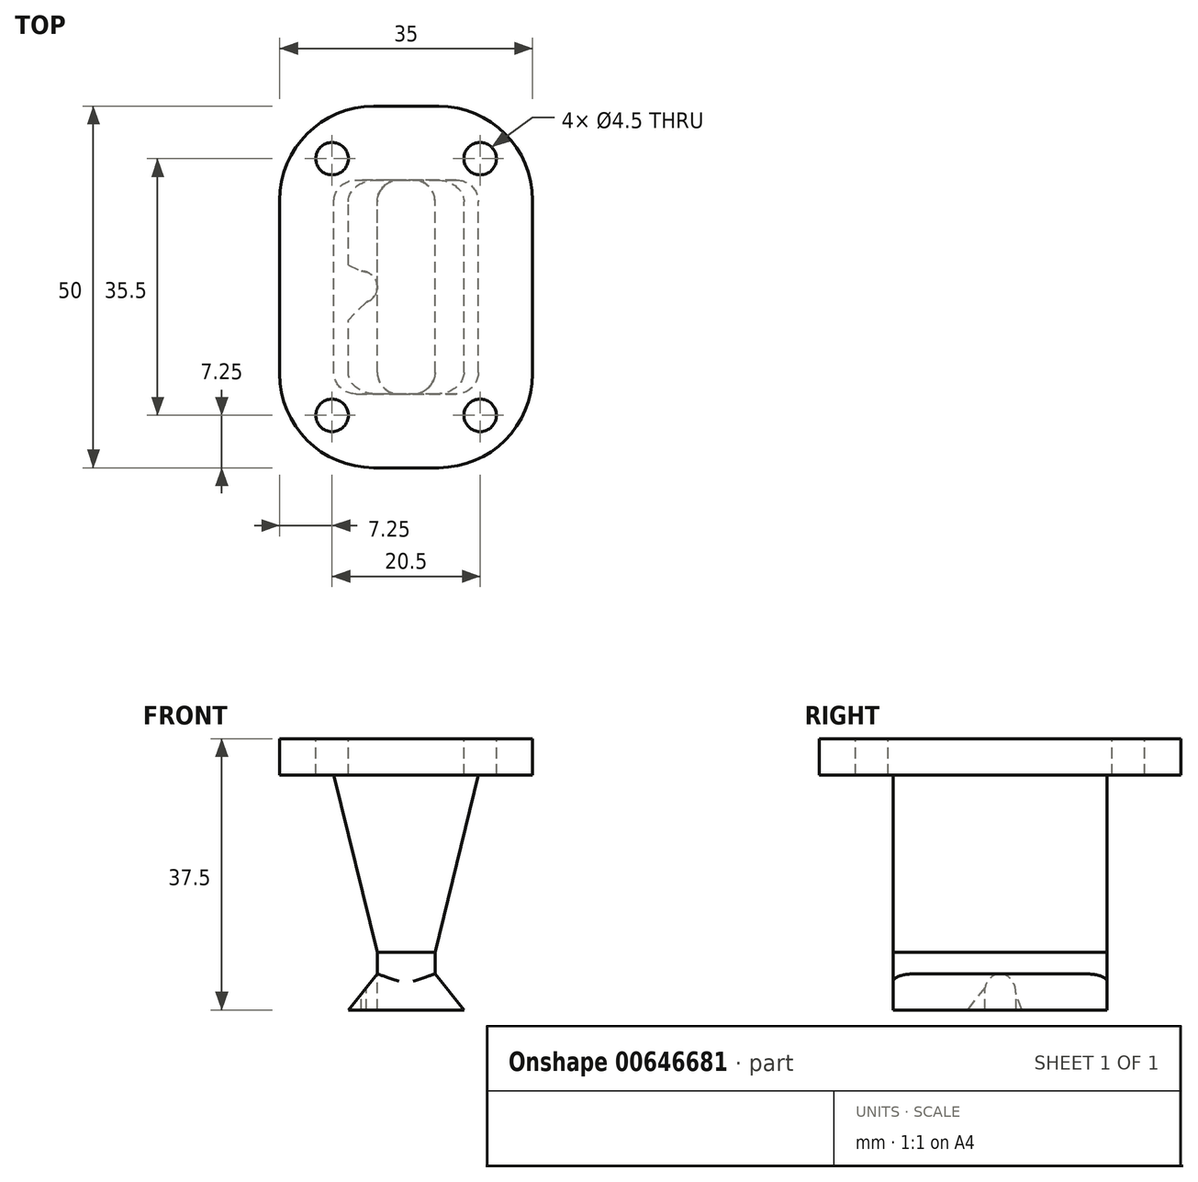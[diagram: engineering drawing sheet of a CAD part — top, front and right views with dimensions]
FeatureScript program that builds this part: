
annotation { "Feature Type Name" : "Feature", "Feature Type Description" : "" }
export const myFeature = defineFeature(function(context is Context, id is Id, definition is map)
    precondition{}
    {
        {
            var Q0;
            Q0=qCreatedBy(makeId("Front.planeOp"),FACE);
            var sketch = newSketch(context, id + "F0", { "sketchPlane" : qUnion([Q0])});
            skLineSegment(sketch, "E0", {"start": v(0, 0) * mm, "end": v(4, 0) * mm});
            skLineSegment(sketch, "E1", {"start": v(0, 0) * mm, "end": v(-4, 0) * mm});
            skLineSegment(sketch, "E2", {"start": v(0, 0) * mm, "end": v(0, -7.5) * mm, "construction": true});
            skLineSegment(sketch, "E3", {"start": v(0, -7.5) * mm, "end": v(8, -7.5) * mm});
            skLineSegment(sketch, "E4", {"start": v(4, 0) * mm, "end": v(4, -2.5) * mm});
            skLineSegment(sketch, "E5", {"start": v(4, -2.5) * mm, "end": v(8, -7.5) * mm});
            skLineSegment(sketch, "E6.MirrorCS", {"start": v(-4, 0) * mm, "end": v(-4, -2.5) * mm});
            skLineSegment(sketch, "E7.MirrorCS", {"start": v(-4, -2.5) * mm, "end": v(-8, -7.5) * mm});
            skLineSegment(sketch, "E8.MirrorCS", {"start": v(0, -7.5) * mm, "end": v(-8, -7.5) * mm});
            skSolve(sketch);
        }
        {
            var Q0;
            Q0=makeQuery(id+"F0.imprint","IMPRINT",FACE,{"disambiguationData":[TD([[makeQuery(id+"F0.imprint","IMPRINT",EDGE,{"derivedFrom":sQuery(id+"F0.wireOp",EDGE,"E0")}),-1.0]])]});
            extrude(context, id + "F1", {"entities" : qUnion([Q0]), "depth" : 29.6 * mm, "offsetDistance" : 25 * mm});
        }
        {
            var Q0;
            Q0=makeQuery(id+"F1.opExtrude","SWEPT_FACE",FACE,{"disambiguationData":[OSD([sQuery(id+"F0.wireOp",EDGE,"E0"),sQuery(id+"F0.wireOp",EDGE,"E1")])]});
            var sketch = newSketch(context, id + "F2", { "sketchPlane" : qUnion([Q0])});
            skLineSegment(sketch, "E9", {"start": v(-4, -14.8) * mm, "end": v(4, -14.8) * mm, "construction": true});
            skLineSegment(sketch, "E10.0", {"start": v(-8, -29.6) * mm, "end": v(-8, 0) * mm, "construction": true});
            skLineSegment(sketch, "E11", {"start": v(-6.2, -14.8) * mm, "end": v(-8, -14.8) * mm, "construction": true});
            skLineSegment(sketch, "E12", {"start": v(-8, -14.8) * mm, "end": v(-8, -18.8) * mm});
            skLineSegment(sketch, "E13", {"start": v(-8, -18.8) * mm, "end": v(-4, -14.8) * mm, "construction": true});
            skLineSegment(sketch, "E14.0", {"start": v(-3.03, -14.4) * mm, "end": v(-4.04, -14.4) * mm, "construction": true});
            skLineSegment(sketch, "E14.1", {"start": v(-8.17, -19.53) * mm, "end": v(-5.53, -16.9) * mm});
            skLineSegment(sketch, "E15", {"start": v(-8, -19.37) * mm, "end": v(-8.17, -19.53) * mm});
            skLineSegment(sketch, "E16", {"start": v(-8, -19.37) * mm, "end": v(-8, -14.4) * mm});
            skLineSegment(sketch, "E17", {"start": v(-4, -14.4) * mm, "end": v(-4, -15.37) * mm});
            skLineSegment(sketch, "E18", {"start": v(-4, -14.8) * mm, "end": v(-6.2, -14.8) * mm});
            skArc(sketch, "E19", {"start": v(-6.2, -17) * mm, "mid": v(-4, -14.8) * mm, "end": v(-6.2, -12.6) * mm});
            skLineSegment(sketch, "E20.trimOffspring", {"start": v(-4.1, -15.47) * mm, "end": v(-3.03, -14.4) * mm, "construction": true});
            skLineSegment(sketch, "E21", {"start": v(-6.2, -14.8) * mm, "end": v(-6.2, -12.6) * mm, "construction": true});
            skLineSegment(sketch, "E22", {"start": v(-9.1, -11.27) * mm, "end": v(-9.1, -19.39) * mm});
            skLineSegment(sketch, "E23", {"start": v(-9.1, -19.39) * mm, "end": v(-8, -19.37) * mm});
            skLineSegment(sketch, "E24", {"start": v(-6.2, -12.6) * mm, "end": v(-9.1, -11.27) * mm});
            skSolve(sketch);
        }
        {
            var Q0;
            {var subQ3=sQuery(id+"F2.wireOp",EDGE,"E14.1");Q0=makeQuery(id+"F2.imprint","IMPRINT",FACE,{"disambiguationData":[TD([[makeQuery(id+"F2.imprint","IMPRINT",EDGE,{"derivedFrom":subQ3}),1.0]])]});}
            extrude(context, id + "F3", {"entities" : qUnion([Q0]), "operationType" : NewBodyOperationType.REMOVE, "oppositeDirection" : true, "depth" : 25 * mm, "offsetDistance" : 25 * mm});
        }
        {
            var Q0;
            {var subQ0=sQuery(id+"F0.wireOp",EDGE,"E0");Q0=makeQuery(id+"F2.imprint","IMPRINT",FACE,{"disambiguationData":[TD([[makeQuery(id+"F2.imprint","IMPRINT",EDGE,{"derivedFrom":makeQuery(id+"F1.opExtrude","SWEPT_EDGE",EDGE,{"disambiguationData":[OSD([subQ0,sQuery(id+"F0.wireOp",EDGE,"E4")])]})}),1.0]])]});}
            cPlane(context, id + "F4", {"entities" : qUnion([Q0]), "cplaneType" : CPlaneType.OFFSET, "offset" : 30 * mm, "width" : 150 * mm, "height" : 150 * mm});
        }
        {
            var Q0;
            Q0=qCreatedBy(id+"F4.planeOp",FACE);
            var sketch = newSketch(context, id + "F5", { "sketchPlane" : qUnion([Q0])});
            skPoint(sketch, "E25.0", {"position": v(0, -14.8) * mm});
            skLineSegment(sketch, "E26.0.1", {"start": v(-4, -15.37) * mm, "end": v(-4, -29.6) * mm, "construction": true});
            skLineSegment(sketch, "E26.0.2", {"start": v(-4, -29.6) * mm, "end": v(4, -29.6) * mm, "construction": true});
            skLineSegment(sketch, "E26.0.3", {"start": v(4, -29.6) * mm, "end": v(4, 0) * mm, "construction": true});
            skLineSegment(sketch, "E26.0.4", {"start": v(4, 0) * mm, "end": v(-4, 0) * mm, "construction": true});
            skLineSegment(sketch, "E26.0.5", {"start": v(-4, 0) * mm, "end": v(-4, -14.4) * mm, "construction": true});
            skLineSegment(sketch, "E27", {"start": v(-4, -14.4) * mm, "end": v(-4, -15.37) * mm, "construction": true});
            skLineSegment(sketch, "E28.bottom", {"start": v(17.5, -39.8) * mm, "end": v(-17.5, -39.8) * mm});
            skLineSegment(sketch, "E28.top", {"start": v(17.5, 10.2) * mm, "end": v(-17.5, 10.2) * mm});
            skLineSegment(sketch, "E28.left", {"start": v(17.5, -39.8) * mm, "end": v(17.5, 10.2) * mm});
            skLineSegment(sketch, "E28.right", {"start": v(-17.5, -39.8) * mm, "end": v(-17.5, 10.2) * mm});
            skLineSegment(sketch, "E29.bottom", {"start": v(8, -30.3) * mm, "end": v(-8, -30.3) * mm, "construction": true});
            skLineSegment(sketch, "E29.top", {"start": v(8, 0.7) * mm, "end": v(-8, 0.7) * mm, "construction": true});
            skLineSegment(sketch, "E29.left", {"start": v(8, -30.3) * mm, "end": v(8, 0.7) * mm, "construction": true});
            skLineSegment(sketch, "E29.right", {"start": v(-8, -30.3) * mm, "end": v(-8, 0.7) * mm, "construction": true});
            skLineSegment(sketch, "E30", {"start": v(8, 0.7) * mm, "end": v(8, 5.2) * mm, "construction": true});
            skLineSegment(sketch, "E31", {"start": v(8, 5.2) * mm, "end": v(12.5, 5.2) * mm, "construction": true});
            skLineSegment(sketch, "E32", {"start": v(12.5, 5.2) * mm, "end": v(12.5, 0.7) * mm, "construction": true});
            skLineSegment(sketch, "E33", {"start": v(12.5, 0.7) * mm, "end": v(8, 0.7) * mm, "construction": true});
            skLineSegment(sketch, "E34", {"start": v(10.25, 5.2) * mm, "end": v(10.25, 0.7) * mm, "construction": true});
            skCircle(sketch, "E35", {"center": v(10.25, 2.95) * mm, "radius": 2.25 * mm});
            skLineSegment(sketch, "E36", {"start": v(0, -14.8) * mm, "end": v(0, -12.15) * mm, "construction": true});
            skLineSegment(sketch, "E37", {"start": v(0, -14.8) * mm, "end": v(2.16, -14.8) * mm, "construction": true});
            skCircle(sketch, "E38.MirrorC", {"center": v(10.25, -32.55) * mm, "radius": 2.25 * mm});
            skCircle(sketch, "E39.MirrorC", {"center": v(-10.25, 2.95) * mm, "radius": 2.25 * mm});
            skCircle(sketch, "E40.MirrorC", {"center": v(-10.25, -32.55) * mm, "radius": 2.25 * mm});
            skSolve(sketch);
        }
        {
            var Q0;
            Q0=makeQuery(id+"F5.imprint","IMPRINT",FACE,{"disambiguationData":[TD([[makeQuery(id+"F5.imprint","IMPRINT",EDGE,{"derivedFrom":sQuery(id+"F5.wireOp",EDGE,"E28.bottom")}),-1.0]])]});
            extrude(context, id + "F6", {"entities" : qUnion([Q0]), "oppositeDirection" : true, "depth" : 5 * mm, "offsetDistance" : 25 * mm});
        }
        {
            var Q0;
            Q0=makeQuery(id+"F6.opExtrude","CAP_FACE",FACE,{"disambiguationData":[OSD([sQuery(id+"F5.wireOp",EDGE,"E28.bottom"),sQuery(id+"F5.wireOp",EDGE,"E28.top"),sQuery(id+"F5.wireOp",EDGE,"E28.left"),sQuery(id+"F5.wireOp",EDGE,"E28.right"),sQuery(id+"F5.wireOp",EDGE,"E35"),sQuery(id+"F5.wireOp",EDGE,"E38.MirrorC"),sQuery(id+"F5.wireOp",EDGE,"E39.MirrorC"),sQuery(id+"F5.wireOp",EDGE,"E40.MirrorC")])],"isStart":false});
            var sketch = newSketch(context, id + "F7", { "sketchPlane" : qUnion([Q0])});
            skLineSegment(sketch, "E41.left", {"start": v(10, 29.6) * mm, "end": v(10, 0) * mm});
            skLineSegment(sketch, "E41.right", {"start": v(-10, 29.6) * mm, "end": v(-10, 0) * mm});
            skPoint(sketch, "E41.middle", {"position": v(0, 14.8) * mm});
            skLineSegment(sketch, "E42", {"start": v(10, 0) * mm, "end": v(-10, 0) * mm});
            skLineSegment(sketch, "E43", {"start": v(10, 29.6) * mm, "end": v(-10, 29.6) * mm});
            skCircle(sketch, "E44", {"center": v(-10.25, -2.95) * mm, "radius": 3.6 * mm, "construction": true});
            skSolve(sketch);
        }
        {
            var Q0;
            {var subQ1=sQuery(id+"F0.wireOp",EDGE,"E0");Q0=makeQuery(id+"F2.imprint","IMPRINT",FACE,{"disambiguationData":[TD([[makeQuery(id+"F2.imprint","IMPRINT",EDGE,{"derivedFrom":makeQuery(id+"F1.opExtrude","SWEPT_EDGE",EDGE,{"disambiguationData":[OSD([subQ1,sQuery(id+"F0.wireOp",EDGE,"E4")])]})}),1.0]])]});}
            var sketch = newSketch(context, id + "F8", { "sketchPlane" : qUnion([Q0])});
            skLineSegment(sketch, "E45.0", {"start": v(0, 0) * mm, "end": v(-4, 0) * mm});
            skLineSegment(sketch, "E46.0", {"start": v(0, 0) * mm, "end": v(4, 0) * mm});
            skLineSegment(sketch, "E47.0", {"start": v(-4, -29.6) * mm, "end": v(4, -29.6) * mm});
            skLineSegment(sketch, "E48.top", {"start": v(-4, 0) * mm, "end": v(4, 0) * mm});
            skLineSegment(sketch, "E48.left", {"start": v(-4, -29.6) * mm, "end": v(-4, 0) * mm});
            skLineSegment(sketch, "E48.right", {"start": v(4, -29.6) * mm, "end": v(4, 0) * mm});
            skSolve(sketch);
        }
        {
            var Q0;
            {var subQ3=sQuery(id+"F8.wireOp",EDGE,"E47.0");Q0=makeQuery(id+"F8.imprint","IMPRINT",FACE,{"disambiguationData":[TD([[makeQuery(id+"F8.imprint","IMPRINT",EDGE,{"derivedFrom":subQ3}),1.0]])]});}
            extrude(context, id + "F9", {"entities" : qUnion([Q0]), "operationType" : NewBodyOperationType.ADD, "depth" : 0.5 * mm, "offsetDistance" : 25 * mm});
        }
        {
            var Q0;
            {var subQ0=sQuery(id+"F7.wireOp",EDGE,"E41.left");Q0=makeQuery(id+"F7.imprint","IMPRINT",FACE,{"disambiguationData":[TD([[makeQuery(id+"F7.imprint","IMPRINT",EDGE,{"derivedFrom":subQ0}),-1.0]])]});}
            var Q1;
            Q1=makeQuery(id+"F9.opExtrude","CAP_FACE",FACE,{"disambiguationData":[OSD([sQuery(id+"F8.wireOp",EDGE,"E47.0"),sQuery(id+"F8.wireOp",EDGE,"E48.top"),sQuery(id+"F8.wireOp",EDGE,"E48.left"),sQuery(id+"F8.wireOp",EDGE,"E48.right")])],"isStart":false});
            loft(context, id + "F10", {"sheetProfilesArray" : [{ "sheetProfileEntities" : qUnion([Q0]) }, { "sheetProfileEntities" : qUnion([Q1]) }]});
        }
        {
            var Q0;
            Q0=makeQuery(id+"F10.opLoft","SWEPT_EDGE",EDGE,{"disambiguationData":[OSD([sQuery(id+"F7.wireOp",EDGE,"E41.right"),sQuery(id+"F7.wireOp",EDGE,"E42"),sQuery(id+"F8.wireOp",EDGE,"E48.top"),sQuery(id+"F8.wireOp",EDGE,"E48.left")])]});
            var Q1;
            Q1=makeQuery(id+"F10.opLoft","SWEPT_EDGE",EDGE,{"disambiguationData":[OSD([sQuery(id+"F7.wireOp",EDGE,"E41.left"),sQuery(id+"F7.wireOp",EDGE,"E42"),sQuery(id+"F8.wireOp",EDGE,"E48.top"),sQuery(id+"F8.wireOp",EDGE,"E48.right")])]});
            var Q2;
            Q2=makeQuery(id+"F9.boolean.opBoolean","MERGE",EDGE,{"derivedFrom":[makeQuery(id+"F1.opExtrude","CAP_EDGE",EDGE,{"disambiguationData":[OSD([sQuery(id+"F0.wireOp",EDGE,"E4")])],"isStart":true}),makeQuery(id+"F9.opExtrude","SWEPT_EDGE",EDGE,{"disambiguationData":[OSD([sQuery(id+"F8.wireOp",EDGE,"E48.top"),sQuery(id+"F8.wireOp",EDGE,"E48.right")])]})]});
            var Q3;
            Q3=makeQuery(id+"F9.boolean.opBoolean","MERGE",EDGE,{"derivedFrom":[makeQuery(id+"F1.opExtrude","CAP_EDGE",EDGE,{"disambiguationData":[OSD([sQuery(id+"F0.wireOp",EDGE,"E6.MirrorCS")])],"isStart":true}),makeQuery(id+"F9.opExtrude","SWEPT_EDGE",EDGE,{"disambiguationData":[OSD([sQuery(id+"F8.wireOp",EDGE,"E48.top"),sQuery(id+"F8.wireOp",EDGE,"E48.left")])]})]});
            var Q4;
            Q4=makeQuery(id+"F1.opExtrude","CAP_EDGE",EDGE,{"disambiguationData":[OSD([sQuery(id+"F0.wireOp",EDGE,"E7.MirrorCS")])],"isStart":true});
            var Q5;
            Q5=makeQuery(id+"F1.opExtrude","CAP_EDGE",EDGE,{"disambiguationData":[OSD([sQuery(id+"F0.wireOp",EDGE,"E5")])],"isStart":true});
            var Q6;
            Q6=makeQuery(id+"F10.opLoft","SWEPT_EDGE",EDGE,{"disambiguationData":[OSD([sQuery(id+"F7.wireOp",EDGE,"E41.bottom"),sQuery(id+"F7.wireOp",EDGE,"E41.left"),sQuery(id+"F8.wireOp",EDGE,"E47.0"),sQuery(id+"F8.wireOp",EDGE,"E48.right")])]});
            var Q7;
            Q7=makeQuery(id+"F10.opLoft","SWEPT_EDGE",EDGE,{"disambiguationData":[OSD([sQuery(id+"F7.wireOp",EDGE,"E41.bottom"),sQuery(id+"F7.wireOp",EDGE,"E41.right"),sQuery(id+"F8.wireOp",EDGE,"E47.0"),sQuery(id+"F8.wireOp",EDGE,"E48.left")])]});
            var Q8;
            Q8=makeQuery(id+"F1.opExtrude","CAP_EDGE",EDGE,{"disambiguationData":[OSD([sQuery(id+"F0.wireOp",EDGE,"E5")])],"isStart":false});
            var Q9;
            Q9=makeQuery(id+"F9.boolean.opBoolean","MERGE",EDGE,{"derivedFrom":[makeQuery(id+"F1.opExtrude","CAP_EDGE",EDGE,{"disambiguationData":[OSD([sQuery(id+"F0.wireOp",EDGE,"E4")])],"isStart":false}),makeQuery(id+"F9.opExtrude","SWEPT_EDGE",EDGE,{"disambiguationData":[OSD([sQuery(id+"F8.wireOp",EDGE,"E47.0"),sQuery(id+"F8.wireOp",EDGE,"E48.right")])]})]});
            var Q10;
            Q10=makeQuery(id+"F9.boolean.opBoolean","MERGE",EDGE,{"derivedFrom":[makeQuery(id+"F1.opExtrude","CAP_EDGE",EDGE,{"disambiguationData":[OSD([sQuery(id+"F0.wireOp",EDGE,"E6.MirrorCS")])],"isStart":false}),makeQuery(id+"F9.opExtrude","SWEPT_EDGE",EDGE,{"disambiguationData":[OSD([sQuery(id+"F8.wireOp",EDGE,"E47.0"),sQuery(id+"F8.wireOp",EDGE,"E48.left")])]})]});
            var Q11;
            Q11=makeQuery(id+"F1.opExtrude","CAP_EDGE",EDGE,{"disambiguationData":[OSD([sQuery(id+"F0.wireOp",EDGE,"E7.MirrorCS")])],"isStart":false});
            fillet(context, id + "F11", {"entities" : qUnion([Q0, Q1, Q2, Q3, Q4, Q5, Q6, Q7, Q8, Q9, Q10, Q11]), "radius" : 3 * mm, "tangentPropagation" : true, "allowEdgeOverflow" : false});
        }
        {
            var Q0;
            Q0=makeQuery(id+"F6.opExtrude","SWEPT_EDGE",EDGE,{"disambiguationData":[OSD([sQuery(id+"F5.wireOp",EDGE,"E28.bottom"),sQuery(id+"F5.wireOp",EDGE,"E28.left")])]});
            var Q1;
            Q1=makeQuery(id+"F6.opExtrude","SWEPT_EDGE",EDGE,{"disambiguationData":[OSD([sQuery(id+"F5.wireOp",EDGE,"E28.top"),sQuery(id+"F5.wireOp",EDGE,"E28.left")])]});
            var Q2;
            Q2=makeQuery(id+"F6.opExtrude","SWEPT_EDGE",EDGE,{"disambiguationData":[OSD([sQuery(id+"F5.wireOp",EDGE,"E28.top"),sQuery(id+"F5.wireOp",EDGE,"E28.right")])]});
            var Q3;
            Q3=makeQuery(id+"F6.opExtrude","SWEPT_EDGE",EDGE,{"disambiguationData":[OSD([sQuery(id+"F5.wireOp",EDGE,"E28.bottom"),sQuery(id+"F5.wireOp",EDGE,"E28.right")])]});
            fillet(context, id + "F12", {"entities" : qUnion([Q0, Q1, Q2, Q3]), "radius" : 13 * mm, "tangentPropagation" : true, "allowEdgeOverflow" : false});
        }
    });
